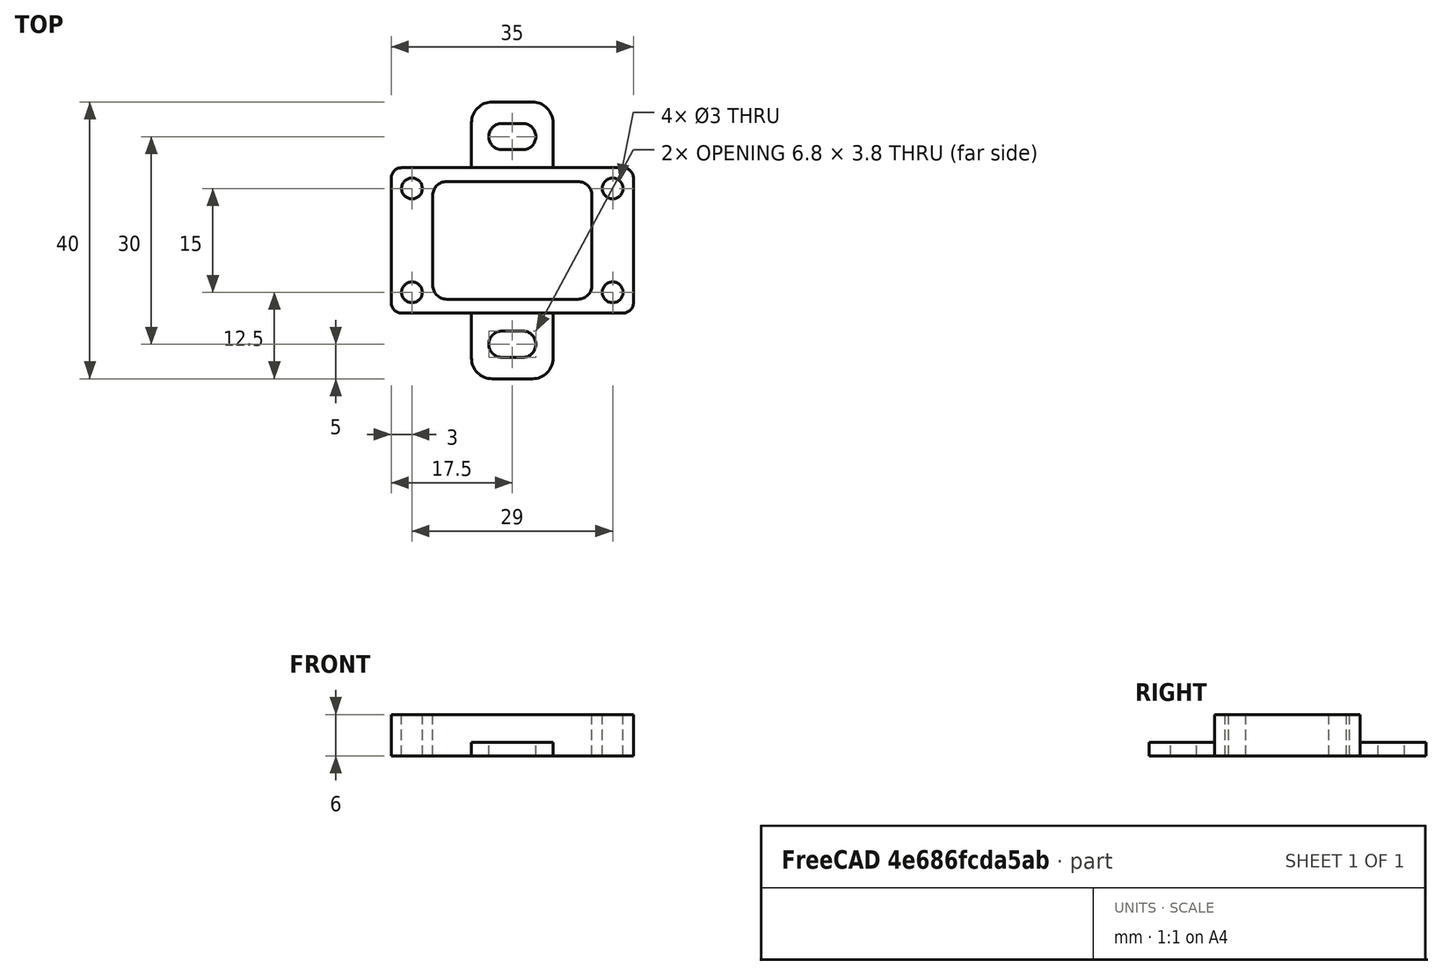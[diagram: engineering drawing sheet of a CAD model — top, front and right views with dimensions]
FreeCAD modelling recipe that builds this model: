
FCSTD DOCUMENT  (FreeCAD 0.19R)
Label: step_up_xl6009e1_hole_dist_29mm
License: All rights reserved
LicenseURL: http://en.wikipedia.org/wiki/All_rights_reserved
objects: Part::Box×2, Part::Fillet×2, Part::MultiFuse×2, Spreadsheet::Sheet×1, Part::Cylinder×1, Part::FeaturePython×1, Part::Feature×1, Part::Cut×1, App::Part×1
note: 10 computed .brp shape members not serialized (recipe doc carries the construction recipe); baked Part::Feature solids carry a one-line shape summary decoded from their .brp

FEATURE [Spreadsheet::Sheet] Spreadsheet  label="p"
  cells = A1=hole_x_dist; B1(hole_x_dist)=29; A2=hole_y_dist; B2(hole_y_dist)=15; A3=pcb_under; B3(pcb_under)=6; A4=pcb_x; B4(pcb_x)=35; A5=pcb_y; B5(pcb_y)=21; A6=hole_r; B6(hole_r)=1.5; A7=under_pcb_border_x; B7(under_pcb_border_x)=6; A8=under_pcb_border_y; B8(under_pcb_border_y)=2
FEATURE [Part::Box] Box  label="bottom cube"
  AttacherType = Attacher::AttachEngine3D
  Height = 6
  Length = 35
  Width = 21
  expr: Height = <<p>>.pcb_under
  expr: Length = <<p>>.pcb_x
  expr: Width = <<p>>.pcb_y
FEATURE [Part::Box] Box001  label="bottom extraction cube"
  AttacherType = Attacher::AttachEngine3D
  Height = 10
  Length = 23
  Placement = pos=(6,2,0) rot=(0,0,1;0rad)
  Width = 17
  expr: Width = <<p>>.pcb_y - <<p>>.under_pcb_border_y * 2
  expr: Length = <<p>>.pcb_x - <<p>>.under_pcb_border_x * 2
  expr: .Placement.Base.x = Spreadsheet.under_pcb_border_x
  expr: .Placement.Base.y = Spreadsheet.under_pcb_border_y
FEATURE [Part::Cylinder] Cylinder  label="pcb hole"
  Angle = 360
  AttacherType = Attacher::AttachEngine3D
  Height = 10
  Radius = 1.5
  expr: Radius = <<p>>.hole_r
FEATURE [Part::FeaturePython] Array001  label="hole array"  # Draft array (typed FeaturePython)
  Angle = 360
  ArrayType = 0
  Axis = (0,0,1)
  Base = -> Cylinder
  Center = (0,0,0)
  Fuse = false
  IntervalAxis = (0,0,0)
  IntervalX = (29,0,0)
  IntervalY = (0,15,0)
  IntervalZ = (0,0,1)
  NumberPolar = 1
  NumberX = 2
  NumberY = 2
  NumberZ = 1
  Placement = pos=(3,3,0) rot=(0,0,1;0rad)
  expr: .Placement.Base.y = (<<p>>.pcb_y - <<p>>.hole_y_dist) / 2
  expr: .Placement.Base.x = (<<p>>.pcb_x - <<p>>.hole_x_dist) / 2
  expr: .IntervalX.x = <<p>>.hole_x_dist
  expr: .IntervalY.y = <<p>>.hole_y_dist
FEATURE [Part::Fillet] Fillet001  label="bottom cube fillet"
  Base = -> Box
  Edges = 4 edges r=1.5: [Edge1,Edge3,Edge5,Edge7]
FEATURE [Part::Fillet] Fillet  label="bottom extraction cube fillet"
  Base = -> Box001
  Edges = 4 edges r=2: [Edge1,Edge3,Edge5,Edge7]
FEATURE [Part::MultiFuse] Fusion  label="bottom extraction"
  Shapes = -> [Array001,Fillet]
FEATURE [Part::Feature] Cut002001  label="attach plane y dir001"
  Placement = pos=(11.6,-9.5,0) rot=(0,0,1;0rad)
  shape: bbox 11.8 x 40 x 2 mm, 20 faces (baked)
FEATURE [Part::MultiFuse] Fusion002  label="bottom fusion"
  Shapes = -> [Fillet001,Cut002001]
FEATURE [Part::Cut] Cut  label="pcb box cut"
  Base = -> Fusion002
  Tool = -> Fusion
FEATURE [App::Part] Part  label="stepup_stepdown part"
  Group = -> [Cut]
  Origin = -> Origin
